# Revit family: 3316R-RegencyCBU-ClusterBoxUnit
name_source: partatom
category: Specialty Equipment
revit_build: Autodesk Revit 2016 (Build: 20150506_1715(x64)
units: mm (PartAtom-declared; Revit-internal decimal feet)

## family parameters
Always vertical = Yes
Cut with Voids When Loaded = No
Host = Floor
Part Type = Normal
Room Calculation Point = No
Round Connector Dimension = Use Diameter
Shared = No
Work Plane-Based = No

## types (1)
- 3316R
    Assembly Code = E1010900
    Depth = 18.425 "
    Description = 16 A Doors, 1 Large Parcel Locker, 1 Small Parcel Locker - Type III - USPS Access
    Door Slot L1 = 3300 Series CBU Door Configurations : A Door
    Door Slot L2 = 3300 Series CBU Door Configurations : A Door w/ Divider
    Door Slot L3 = 3300 Series CBU Door Configurations : A Door w/ Divider
    Door Slot L4 = 3300 Series CBU Door Configurations : A Door w/ Divider
    Door Slot L5 = 3300 Series CBU Door Configurations : A Door
    Door Slot L6 = 3300 Series CBU Door Configurations : A Door w/ Divider
    Door Slot L7 = 3300 Series CBU Door Configurations : A Door w/ Divider
    Door Slot L8 = 3300 Series CBU Door Configurations : A Door w/ Divider
    Door Slot L9 = 3300 Series CBU Parcel Configurations : CBU Large Parcel
    Door Slot R1 = 3300 Series CBU Door Configurations : A Door
    Door Slot R2 = 3300 Series CBU Door Configurations : A Door w/ Divider
    Door Slot R3 = 3300 Series CBU Door Configurations : A Door w/ Divider
    Door Slot R4 = 3300 Series CBU Door Configurations : A Door w/ Divider
    Door Slot R5 = 3300 Series CBU Door Configurations : A Door w/ Divider
    Door Slot R6 = 3300 Series CBU Door Configurations : A Door w/ Divider
    Door Slot R7 = 3300 Series CBU Door Configurations : A Door w/ Divider
    Door Slot R8 = 3300 Series CBU Door Configurations : A Door w/ Divider
    Door Slot R9 = 3300 Series CBU Parcel Configurations : CBU Small Parcel
    Height = 72.105 "
    Lock Material = Stainless Steel -Salsbury Finish =  Polished
    Manufacturer = Salsbury Industries
    MasterFormat Number = 10 55 00
    MasterFormat Title = Postal Specialties
    Model = 3316R
    Type Comments = Regency® Decorative Cluster Box Unit (CBU) - Includes Pedestal
    Version = 1.0 (10/30/15)
    Width = 31.023 "

## geometry (parser evidence)
native form markers: Blend x8, Extrusion x1, Sweep x37
no freeform markers — native parametric forms only
